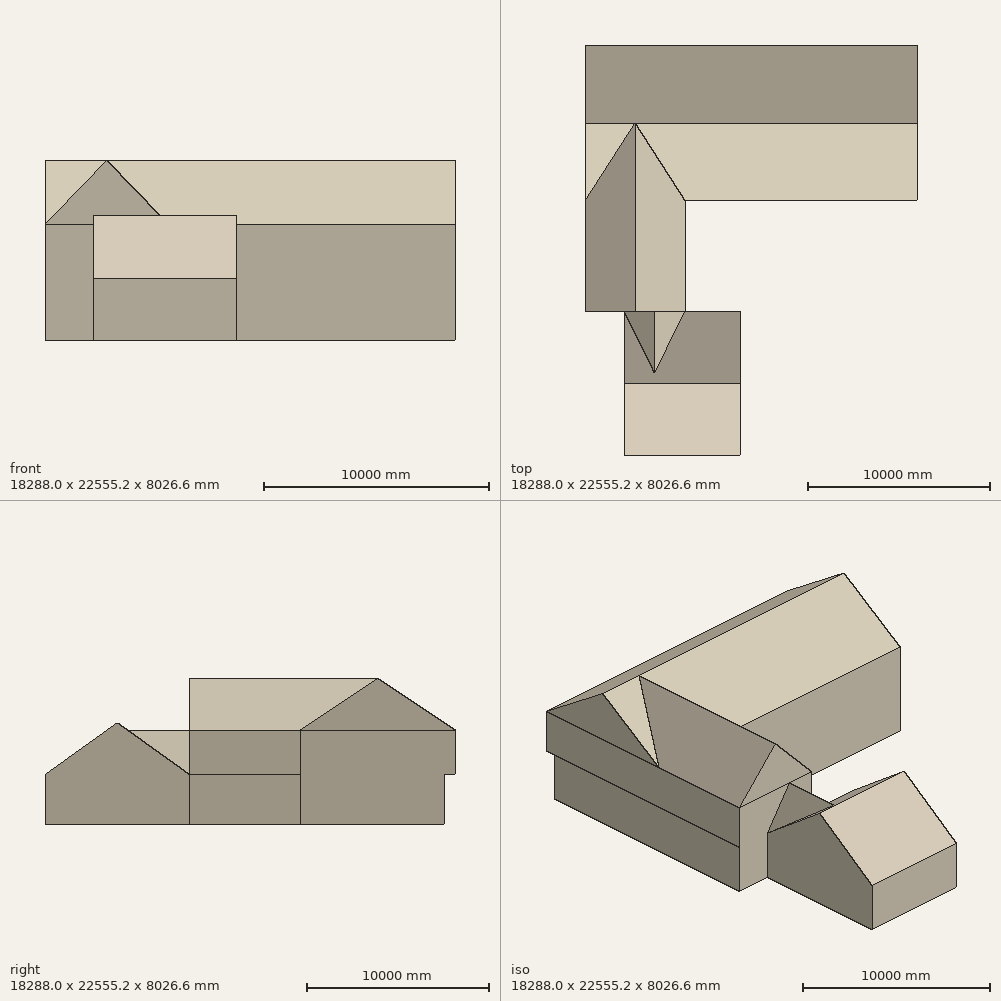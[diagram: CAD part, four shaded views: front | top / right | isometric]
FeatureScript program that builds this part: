
annotation { "Feature Type Name" : "Feature", "Feature Type Description" : "" }
export const myFeature = defineFeature(function(context is Context, id is Id, definition is map)
    precondition{}
    {
        {
            var Q0;
            Q0=qCreatedBy(makeId("Top.planeOp"),FACE);
            var sketch = newSketch(context, id + "F0", { "sketchPlane" : qUnion([Q0])});
            skLineSegment(sketch, "E0.bottom", {"start": v(-6517.2, 12723.03) * mm, "end": v(6284.4, 12723.03) * mm});
            skLineSegment(sketch, "E0.top", {"start": v(-6517.2, 4798.23) * mm, "end": v(6284.4, 4798.23) * mm});
            skLineSegment(sketch, "E0.left", {"start": v(-6517.2, 12723.03) * mm, "end": v(-6517.2, 4798.23) * mm});
            skLineSegment(sketch, "E0.right", {"start": v(6284.4, 12723.03) * mm, "end": v(6284.4, 4798.23) * mm});
            skLineSegment(sketch, "E1.bottom", {"start": v(-3469.2, -1297.77) * mm, "end": v(-9870, -1297.77) * mm});
            skLineSegment(sketch, "E1.top", {"start": v(-3469.2, -9222.57) * mm, "end": v(-9870, -9222.57) * mm});
            skLineSegment(sketch, "E1.left", {"start": v(-3469.2, -1297.77) * mm, "end": v(-3469.2, -9222.57) * mm});
            skLineSegment(sketch, "E1.right", {"start": v(-9870, -1297.77) * mm, "end": v(-9870, -9222.57) * mm});
            skLineSegment(sketch, "E2", {"start": v(-3469.2, -1297.77) * mm, "end": v(-3469.2, 4798.23) * mm});
            skSolve(sketch);
        }
        {
            var Q0;
            Q0=qCreatedBy(makeId("Top.planeOp"),FACE);
            var sketch = newSketch(context, id + "F1", { "sketchPlane" : qUnion([Q0])});
            skLineSegment(sketch, "E3.bottom", {"start": v(-6517.2, 13332.63) * mm, "end": v(6284.4, 13332.63) * mm});
            skLineSegment(sketch, "E3.top", {"start": v(-6517.2, 4798.23) * mm, "end": v(6284.4, 4798.23) * mm});
            skLineSegment(sketch, "E3.left", {"start": v(-6517.2, 13332.63) * mm, "end": v(-6517.2, 4798.23) * mm});
            skLineSegment(sketch, "E3.right", {"start": v(6284.4, 13332.63) * mm, "end": v(6284.4, 4798.23) * mm});
            skSolve(sketch);
        }
        {
            var Q0;
            Q0 = qSketchRegion(id + "F0", true);
            extrude(context, id + "F2", {"entities" : qUnion([Q0]), "depth" : -2743.2 * mm, "offsetDistance" : 25.4 * mm});
        }
        {
            var Q0;
            Q0 = qSketchRegion(id + "F1", true);
            extrude(context, id + "F3", {"entities" : qUnion([Q0]), "operationType" : NewBodyOperationType.ADD, "depth" : 2438.4 * mm, "offsetDistance" : 25.4 * mm});
        }
        {
            var Q0;
            Q0=makeQuery(id+"F3.boolean.opBoolean","MERGE",FACE,{"derivedFrom":[makeQuery(id+"F2.opExtrude","SWEPT_FACE",FACE,{"disambiguationData":[OSD([sQuery(id+"F0.wireOp",EDGE,"E0.right")])]}),makeQuery(id+"F3.opExtrude","SWEPT_FACE",FACE,{"disambiguationData":[OSD([sQuery(id+"F1.wireOp",EDGE,"E3.right")])]})]});
            var sketch = newSketch(context, id + "F4", { "sketchPlane" : qUnion([Q0])});
            skLineSegment(sketch, "E4", {"start": v(4797.92, 2438.6) * mm, "end": v(13332.32, 2438.6) * mm});
            skPoint(sketch, "E5", {"position": v(9065.12, 2438.6) * mm});
            skLineSegment(sketch, "E6", {"start": v(9065.12, 5283.4) * mm, "end": v(4797.92, 2438.6) * mm});
            skLineSegment(sketch, "E7", {"start": v(9065.12, 5283.4) * mm, "end": v(13332.32, 2438.6) * mm});
            skSolve(sketch);
        }
        {
            var Q0;
            Q0 = qSketchRegion(id + "F4", true);
            extrude(context, id + "F5", {"entities" : qUnion([Q0]), "depth" : -18288 * mm, "offsetDistance" : 25.4 * mm});
        }
        {
            var Q0;
            Q0=makeQuery(id+"F2.opExtrude","SWEPT_FACE",FACE,{"disambiguationData":[OSD([sQuery(id+"F0.wireOp",EDGE,"E1.left")])]});
            var sketch = newSketch(context, id + "F6", { "sketchPlane" : qUnion([Q0])});
            skPoint(sketch, "E8", {"position": v(-5260.17, 0) * mm});
            skLineSegment(sketch, "E9.bottom", {"start": v(-9222.57, 0) * mm, "end": v(-1297.77, 0) * mm});
            skLineSegment(sketch, "E9.top", {"start": v(-9222.57, 0) * mm, "end": v(-1297.77, 0) * mm});
            skLineSegment(sketch, "E10", {"start": v(-9222.57, 0) * mm, "end": v(-5260.17, 2844.8) * mm});
            skLineSegment(sketch, "E11", {"start": v(-5260.17, 2844.8) * mm, "end": v(-1297.77, 0) * mm});
            skSolve(sketch);
        }
        {
            var Q0;
            Q0 = qSketchRegion(id + "F6", true);
            extrude(context, id + "F7", {"entities" : qUnion([Q0]), "operationType" : NewBodyOperationType.ADD, "oppositeDirection" : true, "depth" : 6400.8 * mm, "offsetDistance" : 25.4 * mm});
        }
        {
            var Q0;
            Q0=qCreatedBy(makeId("Top.planeOp"),FACE);
            var sketch = newSketch(context, id + "F8", { "sketchPlane" : qUnion([Q0])});
            skLineSegment(sketch, "E12.bottom", {"start": v(-6517.2, 12723.03) * mm, "end": v(-12003.6, 12723.03) * mm});
            skLineSegment(sketch, "E12.top", {"start": v(-6517.2, -1297.77) * mm, "end": v(-12003.6, -1297.77) * mm});
            skLineSegment(sketch, "E12.left", {"start": v(-6517.2, 12723.03) * mm, "end": v(-6517.2, -1297.77) * mm});
            skLineSegment(sketch, "E12.right", {"start": v(-12003.6, 12723.03) * mm, "end": v(-12003.6, -1297.77) * mm});
            skSolve(sketch);
        }
        {
            var Q0;
            Q0 = qSketchRegion(id + "F8", true);
            extrude(context, id + "F9", {"entities" : qUnion([Q0]), "depth" : -2743.2 * mm, "offsetDistance" : 25.4 * mm});
        }
        {
            var Q0;
            Q0=qCreatedBy(makeId("Top.planeOp"),FACE);
            var sketch = newSketch(context, id + "F10", { "sketchPlane" : qUnion([Q0])});
            skLineSegment(sketch, "E13.bottom", {"start": v(-6516.01, 13332.63) * mm, "end": v(-12002.41, 13332.63) * mm});
            skLineSegment(sketch, "E13.top", {"start": v(-6516.01, -1297.77) * mm, "end": v(-12002.41, -1297.77) * mm});
            skLineSegment(sketch, "E13.left", {"start": v(-6516.01, 13332.63) * mm, "end": v(-6516.01, -1297.77) * mm});
            skLineSegment(sketch, "E13.right", {"start": v(-12002.41, 13332.63) * mm, "end": v(-12002.41, -1297.77) * mm});
            skSolve(sketch);
        }
        {
            var Q0;
            Q0 = qSketchRegion(id + "F10", true);
            extrude(context, id + "F11", {"entities" : qUnion([Q0]), "operationType" : NewBodyOperationType.ADD, "depth" : 2438.4 * mm, "offsetDistance" : 25.4 * mm});
        }
        {
            var Q0;
            Q0=makeQuery(id+"F11.boolean.opBoolean","MERGE",FACE,{"derivedFrom":[makeQuery(id+"F9.opExtrude","SWEPT_FACE",FACE,{"disambiguationData":[OSD([sQuery(id+"F8.wireOp",EDGE,"E12.top")])]}),makeQuery(id+"F11.opExtrude","SWEPT_FACE",FACE,{"disambiguationData":[OSD([sQuery(id+"F10.wireOp",EDGE,"E13.top")])]})]});
            var sketch = newSketch(context, id + "F12", { "sketchPlane" : qUnion([Q0])});
            skLineSegment(sketch, "E14", {"start": v(-12002.41, 2438.4) * mm, "end": v(-6516.01, 2438.4) * mm});
            skLineSegment(sketch, "E15", {"start": v(-6516.01, 2438.4) * mm, "end": v(-9259.21, 5283.2) * mm});
            skLineSegment(sketch, "E16", {"start": v(-9259.21, 5283.2) * mm, "end": v(-12002.41, 2438.4) * mm});
            skSolve(sketch);
        }
        {
            var Q0;
            Q0 = qSketchRegion(id + "F12", true);
            extrude(context, id + "F13", {"entities" : qUnion([Q0]), "oppositeDirection" : true, "depth" : 10388.6 * mm, "offsetDistance" : 25.4 * mm});
        }
        {
            var Q0;
            Q0=makeQuery(id+"F11.boolean.opBoolean","MERGE",FACE,{"derivedFrom":[makeQuery(id+"F9.opExtrude","SWEPT_FACE",FACE,{"disambiguationData":[OSD([sQuery(id+"F8.wireOp",EDGE,"E12.top")])]}),makeQuery(id+"F11.opExtrude","SWEPT_FACE",FACE,{"disambiguationData":[OSD([sQuery(id+"F10.wireOp",EDGE,"E13.top")])]})]});
            var sketch = newSketch(context, id + "F14", { "sketchPlane" : qUnion([Q0])});
            skLineSegment(sketch, "E17", {"start": v(-6516.01, 0) * mm, "end": v(-9868.81, 0) * mm});
            skLineSegment(sketch, "E18", {"start": v(-9868.81, 0) * mm, "end": v(-8192.41, 2438.4) * mm});
            skLineSegment(sketch, "E19", {"start": v(-8192.41, 2438.4) * mm, "end": v(-6516.01, 0) * mm});
            skSolve(sketch);
        }
        {
            var Q0;
            Q0 = qSketchRegion(id + "F14", true);
            extrude(context, id + "F15", {"entities" : qUnion([Q0]), "depth" : 3632.2 * mm, "offsetDistance" : 25.4 * mm});
        }
    });
